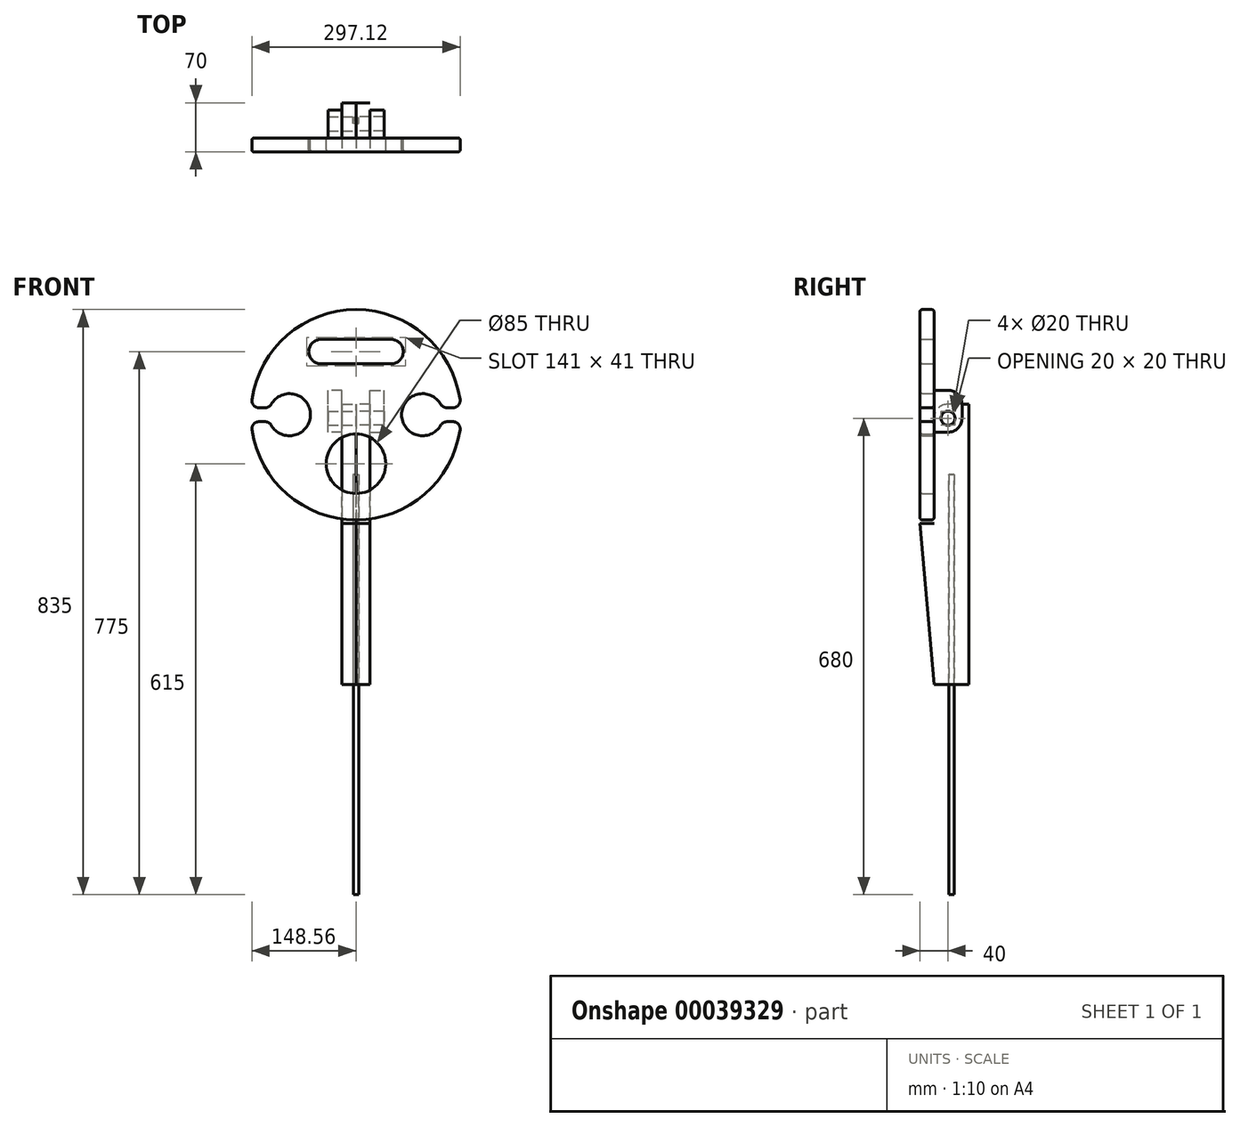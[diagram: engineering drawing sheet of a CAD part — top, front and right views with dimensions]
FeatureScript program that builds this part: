
annotation { "Feature Type Name" : "Feature", "Feature Type Description" : "" }
export const myFeature = defineFeature(function(context is Context, id is Id, definition is map)
    precondition{}
    {
        {
            var Q0;
            Q0=qCreatedBy(makeId("Top.planeOp"),FACE);
            var sketch = newSketch(context, id + "F0", { "sketchPlane" : qUnion([Q0])});
            skCircle(sketch, "E0", {"center": v(0, 0) * mm, "radius": 150 * mm});
            skCircle(sketch, "E1", {"center": v(-50, 90) * mm, "radius": 17.5 * mm});
            skCircle(sketch, "E2", {"center": v(50, 90) * mm, "radius": 17.5 * mm});
            skLineSegment(sketch, "E3", {"start": v(-50, 107.5) * mm, "end": v(50, 107.5) * mm});
            skLineSegment(sketch, "E4", {"start": v(50, 72.5) * mm, "end": v(-50, 72.5) * mm});
            skCircle(sketch, "E5", {"center": v(0, -70) * mm, "radius": 42.5 * mm});
            skCircle(sketch, "E6", {"center": v(-95, 0) * mm, "radius": 30 * mm});
            skCircle(sketch, "E7", {"center": v(95, 0) * mm, "radius": 30 * mm});
            skLineSegment(sketch, "E8", {"start": v(123.28, 10) * mm, "end": v(149.67, 10) * mm});
            skLineSegment(sketch, "E9", {"start": v(123.28, -10) * mm, "end": v(149.67, -10) * mm});
            skLineSegment(sketch, "E10", {"start": v(-123.28, 10) * mm, "end": v(-149.67, 10) * mm});
            skLineSegment(sketch, "E11", {"start": v(-123.28, -10) * mm, "end": v(-149.67, -10) * mm});
            skSolve(sketch);
        }
        {
            var Q0;
            Q0=makeQuery(id+"F0.imprint","IMPRINT",FACE,{"disambiguationData":[TD([[makeQuery(id+"F0.imprint","IMPRINT",EDGE,{"derivedFrom":sQuery(id+"F0.wireOp",EDGE,"E0")}),1.0]])]});
            extrude(context, id + "F1", {"entities" : qUnion([Q0]), "depth" : 20 * mm});
        }
        {
            var Q0;
            Q0=makeQuery(id+"F1.opExtrude","SWEPT_EDGE",EDGE,{"disambiguationData":[OSD([sQuery(id+"F0.wireOp",EDGE,"E6"),sQuery(id+"F0.wireOp",EDGE,"E10")])]});
            var Q1;
            Q1=makeQuery(id+"F1.opExtrude","SWEPT_EDGE",EDGE,{"disambiguationData":[OSD([sQuery(id+"F0.wireOp",EDGE,"E6"),sQuery(id+"F0.wireOp",EDGE,"E11")])]});
            var Q2;
            Q2=makeQuery(id+"F1.opExtrude","SWEPT_EDGE",EDGE,{"disambiguationData":[OSD([sQuery(id+"F0.wireOp",EDGE,"E7"),sQuery(id+"F0.wireOp",EDGE,"E9")])]});
            var Q3;
            Q3=makeQuery(id+"F1.opExtrude","SWEPT_EDGE",EDGE,{"disambiguationData":[OSD([sQuery(id+"F0.wireOp",EDGE,"E7"),sQuery(id+"F0.wireOp",EDGE,"E8")])]});
            fillet(context, id + "F2", {"entities" : qUnion([Q0, Q1, Q2, Q3]), "radius" : 10 * mm, "tangentPropagation" : true, "allowEdgeOverflow" : false});
        }
        {
            var Q0;
            Q0=makeQuery(id+"F1.opExtrude","SWEPT_EDGE",EDGE,{"disambiguationData":[OSD([sQuery(id+"F0.wireOp",EDGE,"E0"),sQuery(id+"F0.wireOp",EDGE,"E10")])]});
            var Q1;
            Q1=makeQuery(id+"F1.opExtrude","SWEPT_EDGE",EDGE,{"disambiguationData":[OSD([sQuery(id+"F0.wireOp",EDGE,"E0"),sQuery(id+"F0.wireOp",EDGE,"E11")])]});
            var Q2;
            Q2=makeQuery(id+"F1.opExtrude","SWEPT_EDGE",EDGE,{"disambiguationData":[OSD([sQuery(id+"F0.wireOp",EDGE,"E0"),sQuery(id+"F0.wireOp",EDGE,"E8")])]});
            var Q3;
            Q3=makeQuery(id+"F1.opExtrude","SWEPT_EDGE",EDGE,{"disambiguationData":[OSD([sQuery(id+"F0.wireOp",EDGE,"E0"),sQuery(id+"F0.wireOp",EDGE,"E9")])]});
            fillet(context, id + "F3", {"entities" : qUnion([Q0, Q1, Q2, Q3]), "radius" : 10 * mm, "tangentPropagation" : true, "allowEdgeOverflow" : false});
        }
        {
            var Q0;
            Q0=qCreatedBy(makeId("Right.planeOp"),FACE);
            var sketch = newSketch(context, id + "F4", { "sketchPlane" : qUnion([Q0])});
            skLineSegment(sketch, "E12", {"start": v(-25, 0) * mm, "end": v(-25, -170) * mm});
            skLineSegment(sketch, "E13", {"start": v(-25, -170) * mm, "end": v(-45, -170) * mm});
            skLineSegment(sketch, "E14", {"start": v(-45, -170) * mm, "end": v(-25, -400) * mm});
            skLineSegment(sketch, "E15", {"start": v(-25, -400) * mm, "end": v(25, -400) * mm});
            skLineSegment(sketch, "E16", {"start": v(25, -400) * mm, "end": v(25, 0) * mm});
            skLineSegment(sketch, "E17", {"start": v(25, 0) * mm, "end": v(-25, 0) * mm});
            skSolve(sketch);
        }
        {
            var Q0;
            Q0=makeQuery(id+"F4.imprint","IMPRINT",FACE,{"disambiguationData":[TD([[makeQuery(id+"F4.imprint","IMPRINT",EDGE,{"derivedFrom":sQuery(id+"F4.wireOp",EDGE,"E12")}),1.0]])]});
            extrude(context, id + "F5", {"entities" : qUnion([Q0]), "depth" : 20 * mm});
        }
        {
            var Q0;
            Q0=makeQuery(id+"F5.opExtrude","SWEPT_FACE",FACE,{"disambiguationData":[OSD([sQuery(id+"F4.wireOp",EDGE,"E15")])]});
            var sketch = newSketch(context, id + "F6", { "sketchPlane" : qUnion([Q0])});
            skLineSegment(sketch, "E18.bottom", {"start": v(0, 4) * mm, "end": v(4, 4) * mm});
            skLineSegment(sketch, "E18.top", {"start": v(0, -4) * mm, "end": v(4, -4) * mm});
            skLineSegment(sketch, "E18.left", {"start": v(0, 4) * mm, "end": v(0, -4) * mm});
            skLineSegment(sketch, "E18.right", {"start": v(4, 4) * mm, "end": v(4, -4) * mm});
            skSolve(sketch);
        }
        {
            var Q0;
            Q0=makeQuery(id+"F6.imprint","IMPRINT",FACE,{"disambiguationData":[TD([[makeQuery(id+"F6.imprint","IMPRINT",EDGE,{"derivedFrom":sQuery(id+"F6.wireOp",EDGE,"E18.bottom")}),-1.0]])]});
            extrude(context, id + "F7", {"entities" : qUnion([Q0]), "operationType" : NewBodyOperationType.REMOVE, "oppositeDirection" : true, "depth" : 300 * mm});
        }
        {
            var Q0;
            Q0=makeQuery(id+"F5.opExtrude","SWEPT_EDGE",EDGE,{"disambiguationData":[OSD([sQuery(id+"F4.wireOp",EDGE,"E12"),sQuery(id+"F4.wireOp",EDGE,"E17")])]});
            fillet(context, id + "F8", {"entities" : qUnion([Q0]), "radius" : 20 * mm, "tangentPropagation" : true, "allowEdgeOverflow" : false});
        }
        {
            var Q0;
            Q0=makeQuery(id+"F5.opExtrude","CAP_FACE",FACE,{"disambiguationData":[OSD([sQuery(id+"F4.wireOp",EDGE,"E12"),sQuery(id+"F4.wireOp",EDGE,"E13"),sQuery(id+"F4.wireOp",EDGE,"E14"),sQuery(id+"F4.wireOp",EDGE,"E15"),sQuery(id+"F4.wireOp",EDGE,"E16"),sQuery(id+"F4.wireOp",EDGE,"E17")])],"isStart":true});
            var sketch = newSketch(context, id + "F9", { "sketchPlane" : qUnion([Q0])});
            skCircle(sketch, "E19", {"center": v(5, -20) * mm, "radius": 10 * mm});
            skSolve(sketch);
        }
        {
            var Q0;
            Q0=makeQuery(id+"F9.imprint","IMPRINT",FACE,{"disambiguationData":[TD([[makeQuery(id+"F9.imprint","IMPRINT",EDGE,{"derivedFrom":sQuery(id+"F9.wireOp",EDGE,"E19")}),1.0]])]});
            extrude(context, id + "F10", {"entities" : qUnion([Q0]), "operationType" : NewBodyOperationType.REMOVE, "endBound" : BoundingType.UP_TO_NEXT, "oppositeDirection" : true, "depth" : 25 * mm});
        }
        {
            var Q0;
            Q0=makeQuery(id+"F5.opExtrude","SWEPT_BODY",BODY,{"disambiguationData":[OSD([sQuery(id+"F4.wireOp",EDGE,"E12"),sQuery(id+"F4.wireOp",EDGE,"E13"),sQuery(id+"F4.wireOp",EDGE,"E14"),sQuery(id+"F4.wireOp",EDGE,"E15"),sQuery(id+"F4.wireOp",EDGE,"E16"),sQuery(id+"F4.wireOp",EDGE,"E17")])]});
            var Q1;
            Q1=makeQuery(id+"F5.opExtrude","CAP_FACE",FACE,{"disambiguationData":[OSD([sQuery(id+"F4.wireOp",EDGE,"E12"),sQuery(id+"F4.wireOp",EDGE,"E13"),sQuery(id+"F4.wireOp",EDGE,"E14"),sQuery(id+"F4.wireOp",EDGE,"E15"),sQuery(id+"F4.wireOp",EDGE,"E16"),sQuery(id+"F4.wireOp",EDGE,"E17")])],"isStart":true});
            mirror(context, id + "F11", {"entities" : qUnion([Q0]), "mirrorPlane" : qUnion([Q1])});
        }
        {
            var Q0;
            Q0=makeQuery(id+"F1.opExtrude","CAP_FACE",FACE,{"disambiguationData":[OSD([sQuery(id+"F0.wireOp",EDGE,"E0"),sQuery(id+"F0.wireOp",EDGE,"E1"),sQuery(id+"F0.wireOp",EDGE,"E2"),sQuery(id+"F0.wireOp",EDGE,"E3"),sQuery(id+"F0.wireOp",EDGE,"E4"),sQuery(id+"F0.wireOp",EDGE,"E5"),sQuery(id+"F0.wireOp",EDGE,"E6"),sQuery(id+"F0.wireOp",EDGE,"E7"),sQuery(id+"F0.wireOp",EDGE,"E8"),sQuery(id+"F0.wireOp",EDGE,"E9"),sQuery(id+"F0.wireOp",EDGE,"E10"),sQuery(id+"F0.wireOp",EDGE,"E11")])],"isStart":true});
            var sketch = newSketch(context, id + "F12", { "sketchPlane" : qUnion([Q0])});
            skLineSegment(sketch, "E20.bottom", {"start": v(-20, 25) * mm, "end": v(-40, 25) * mm});
            skLineSegment(sketch, "E20.top", {"start": v(-20, -35) * mm, "end": v(-40, -35) * mm});
            skLineSegment(sketch, "E20.left", {"start": v(-20, 25) * mm, "end": v(-20, -35) * mm});
            skLineSegment(sketch, "E20.right", {"start": v(-40, 25) * mm, "end": v(-40, -35) * mm});
            skSolve(sketch);
        }
        {
            var Q0;
            Q0=makeQuery(id+"F12.imprint","IMPRINT",FACE,{"disambiguationData":[TD([[makeQuery(id+"F12.imprint","IMPRINT",EDGE,{"derivedFrom":sQuery(id+"F12.wireOp",EDGE,"E20.bottom")}),1.0]])]});
            extrude(context, id + "F13", {"entities" : qUnion([Q0]), "depth" : 40 * mm});
        }
        {
            var Q0;
            Q0=makeQuery(id+"F9.imprint","IMPRINT",FACE,{"disambiguationData":[TD([[makeQuery(id+"F9.imprint","IMPRINT",EDGE,{"derivedFrom":sQuery(id+"F9.wireOp",EDGE,"E19")}),1.0]])]});
            extrude(context, id + "F14", {"entities" : qUnion([Q0]), "operationType" : NewBodyOperationType.REMOVE, "endBound" : BoundingType.THROUGH_ALL, "depth" : 25 * mm});
        }
        {
            var Q0;
            Q0=makeQuery(id+"F13.opExtrude","CAP_EDGE",EDGE,{"disambiguationData":[OSD([sQuery(id+"F12.wireOp",EDGE,"E20.bottom")])],"isStart":false});
            var Q1;
            Q1=makeQuery(id+"F13.opExtrude","CAP_EDGE",EDGE,{"disambiguationData":[OSD([sQuery(id+"F12.wireOp",EDGE,"E20.top")])],"isStart":false});
            fillet(context, id + "F15", {"entities" : qUnion([Q0, Q1]), "radius" : 20 * mm, "tangentPropagation" : true, "allowEdgeOverflow" : false});
        }
        {
            var Q0;
            Q0=makeQuery(id+"F13.opExtrude","SWEPT_BODY",BODY,{"disambiguationData":[OSD([sQuery(id+"F12.wireOp",EDGE,"E20.bottom"),sQuery(id+"F12.wireOp",EDGE,"E20.top"),sQuery(id+"F12.wireOp",EDGE,"E20.left"),sQuery(id+"F12.wireOp",EDGE,"E20.right")])]});
            var Q1;
            Q1=qCreatedBy(makeId("Right.planeOp"),FACE);
            mirror(context, id + "F16", {"entities" : qUnion([Q0]), "mirrorPlane" : qUnion([Q1])});
        }
        {
            var Q0;
            {var subQ0=sQuery(id+"F0.wireOp",EDGE,"E0");Q0=makeQuery(id+"F1.opExtrude","CAP_EDGE",EDGE,{"disambiguationData":[OSD([subQ0]),TDD([makeQuery(id+"F0.imprint","IMPRINT",EDGE,{"disambiguationData":[TD([[makeQuery(id+"F0.imprint","INTERSECT",VERTEX,{"derivedFrom":[subQ0,sQuery(id+"F0.wireOp",EDGE,"E9")]}),1.0]])],"derivedFrom":subQ0})])],"isStart":true});}
            var Q1;
            {var subQ0=sQuery(id+"F0.wireOp",EDGE,"E0");Q1=makeQuery(id+"F1.opExtrude","CAP_EDGE",EDGE,{"disambiguationData":[OSD([subQ0]),TDD([makeQuery(id+"F0.imprint","IMPRINT",EDGE,{"disambiguationData":[TD([[makeQuery(id+"F0.imprint","INTERSECT",VERTEX,{"derivedFrom":[subQ0,sQuery(id+"F0.wireOp",EDGE,"E9")]}),1.0]])],"derivedFrom":subQ0})])],"isStart":false});}
            var Q2;
            Q2=makeQuery(id+"F1.opExtrude","CAP_EDGE",EDGE,{"disambiguationData":[OSD([sQuery(id+"F0.wireOp",EDGE,"E5")])],"isStart":false});
            var Q3;
            Q3=makeQuery(id+"F1.opExtrude","CAP_EDGE",EDGE,{"disambiguationData":[OSD([sQuery(id+"F0.wireOp",EDGE,"E5")])],"isStart":true});
            var Q4;
            Q4=makeQuery(id+"F1.opExtrude","CAP_EDGE",EDGE,{"disambiguationData":[OSD([sQuery(id+"F0.wireOp",EDGE,"E3")])],"isStart":false});
            var Q5;
            Q5=makeQuery(id+"F1.opExtrude","CAP_EDGE",EDGE,{"disambiguationData":[OSD([sQuery(id+"F0.wireOp",EDGE,"E3")])],"isStart":true});
            fillet(context, id + "F17", {"entities" : qUnion([Q0, Q1, Q2, Q3, Q4, Q5]), "radius" : 3 * mm, "tangentPropagation" : true, "allowEdgeOverflow" : false});
        }
        {
            var Q0;
            Q0=makeQuery(id+"F7.boolean.opBoolean","COPY",FACE,{"derivedFrom":makeQuery(id+"F7.opExtrude","CAP_FACE",FACE,{"disambiguationData":[OSD([sQuery(id+"F6.wireOp",EDGE,"E18.bottom"),sQuery(id+"F6.wireOp",EDGE,"E18.top"),sQuery(id+"F6.wireOp",EDGE,"E18.left"),sQuery(id+"F6.wireOp",EDGE,"E18.right")])],"isStart":false})});
            var sketch = newSketch(context, id + "F18", { "sketchPlane" : qUnion([Q0])});
            skCircle(sketch, "E21", {"center": v(0.07, 0) * mm, "radius": 4 * mm});
            skPoint(sketch, "E21.first.point", {"position": v(0, 4) * mm});
            skPoint(sketch, "E21.second.point", {"position": v(0, -4) * mm});
            skPoint(sketch, "E21.third.point", {"position": v(4, -0.72) * mm});
            skSolve(sketch);
        }
        {
            var Q0;
            Q0 = qSketchRegion(id + "F18", true);
            extrude(context, id + "F19", {"entities" : qUnion([Q0]), "depth" : 600 * mm});
        }
        {
            var Q0;
            Q0=makeQuery(id+"F1.opExtrude","SWEPT_BODY",BODY,{"disambiguationData":[OSD([sQuery(id+"F0.wireOp",EDGE,"E0"),sQuery(id+"F0.wireOp",EDGE,"E1"),sQuery(id+"F0.wireOp",EDGE,"E2"),sQuery(id+"F0.wireOp",EDGE,"E3"),sQuery(id+"F0.wireOp",EDGE,"E4"),sQuery(id+"F0.wireOp",EDGE,"E5"),sQuery(id+"F0.wireOp",EDGE,"E6"),sQuery(id+"F0.wireOp",EDGE,"E7"),sQuery(id+"F0.wireOp",EDGE,"E8"),sQuery(id+"F0.wireOp",EDGE,"E9"),sQuery(id+"F0.wireOp",EDGE,"E10"),sQuery(id+"F0.wireOp",EDGE,"E11")])]});
            var Q1;
            Q1=makeQuery(id+"F16.opPattern","COPY",BODY,{"derivedFrom":makeQuery(id+"F13.opExtrude","SWEPT_BODY",BODY,{"disambiguationData":[OSD([sQuery(id+"F12.wireOp",EDGE,"E20.bottom"),sQuery(id+"F12.wireOp",EDGE,"E20.top"),sQuery(id+"F12.wireOp",EDGE,"E20.left"),sQuery(id+"F12.wireOp",EDGE,"E20.right")])]}),"instanceName":"1"});
            var Q2;
            Q2=makeQuery(id+"F13.opExtrude","SWEPT_BODY",BODY,{"disambiguationData":[OSD([sQuery(id+"F12.wireOp",EDGE,"E20.bottom"),sQuery(id+"F12.wireOp",EDGE,"E20.top"),sQuery(id+"F12.wireOp",EDGE,"E20.left"),sQuery(id+"F12.wireOp",EDGE,"E20.right")])]});
            var Q3;
            Q3=makeQuery(id+"F16.opPattern","COPY",FACE,{"derivedFrom":makeQuery(id+"F14.boolean.opBoolean","COPY",FACE,{"derivedFrom":makeQuery(id+"F14.opExtrude","SWEPT_FACE",FACE,{"disambiguationData":[OSD([sQuery(id+"F9.wireOp",EDGE,"E19")])]})}),"instanceName":"1"});
            transform(context, id + "F20", {"entities" : qUnion([Q0, Q1, Q2]), "transformType" : TransformType.ROTATION, "transformAxis" : qUnion([Q3]), "angle" : 90 * degree, "makeCopy" : false});
        }
    });
